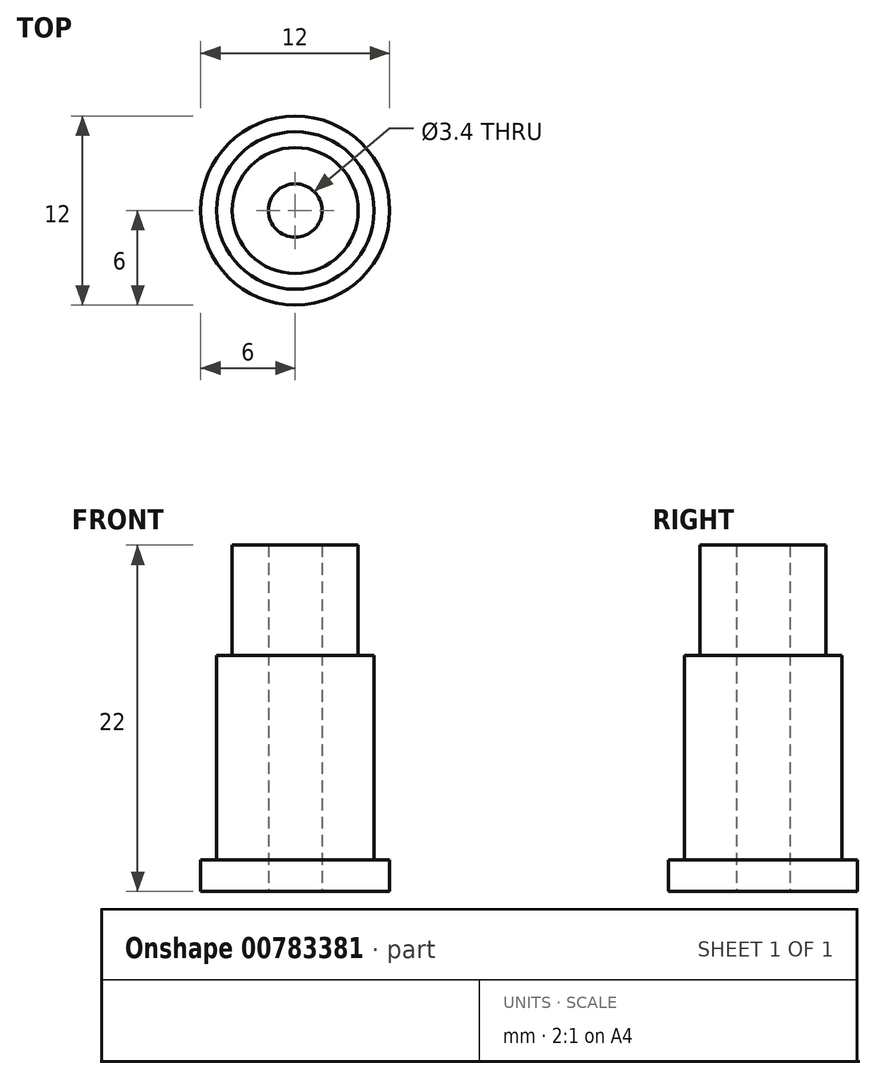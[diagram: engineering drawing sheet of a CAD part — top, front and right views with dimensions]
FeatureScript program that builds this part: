
annotation { "Feature Type Name" : "Feature", "Feature Type Description" : "" }
export const myFeature = defineFeature(function(context is Context, id is Id, definition is map)
    precondition{}
    {
        {
            var Q0;
            Q0=qCreatedBy(makeId("Top.planeOp"),FACE);
            var sketch = newSketch(context, id + "F0", { "sketchPlane" : qUnion([Q0])});
            skCircle(sketch, "E0", {"center": v(0, 0) * mm, "radius": 5 * mm});
            skCircle(sketch, "E1", {"center": v(0, 0) * mm, "radius": 4 * mm});
            skCircle(sketch, "E2", {"center": v(0, 0) * mm, "radius": 6 * mm});
            skSolve(sketch);
        }
        {
            var Q0;
            Q0=makeQuery(id+"F0.imprint","IMPRINT",FACE,{"disambiguationData":[TD([[makeQuery(id+"F0.imprint","IMPRINT",EDGE,{"derivedFrom":sQuery(id+"F0.wireOp",EDGE,"E1")}),1.0]])]});
            extrude(context, id + "F1", {"entities" : qUnion([Q0]), "depth" : 22 * mm, "offsetDistance" : 25 * mm});
        }
        {
            var Q0;
            Q0=makeQuery(id+"F0.imprint","IMPRINT",FACE,{"disambiguationData":[TD([[makeQuery(id+"F0.imprint","IMPRINT",EDGE,{"derivedFrom":sQuery(id+"F0.wireOp",EDGE,"E0")}),1.0]])]});
            extrude(context, id + "F2", {"entities" : qUnion([Q0]), "operationType" : NewBodyOperationType.ADD, "depth" : 15 * mm, "offsetDistance" : 25 * mm});
        }
        {
            var Q0;
            Q0=makeQuery(id+"F0.imprint","IMPRINT",FACE,{"disambiguationData":[TD([[makeQuery(id+"F0.imprint","IMPRINT",EDGE,{"derivedFrom":sQuery(id+"F0.wireOp",EDGE,"E0")}),-1.0]])]});
            extrude(context, id + "F3", {"entities" : qUnion([Q0]), "operationType" : NewBodyOperationType.ADD, "depth" : 2 * mm, "offsetDistance" : 25 * mm});
        }
        {
            var Q0;
            Q0=sQuery(id+"F0.wireOp",VERTEX,"E0.center");
            var Q1;
            Q1=makeQuery(id+"F1.opExtrude","SWEPT_BODY",BODY,{"disambiguationData":[OSD([sQuery(id+"F0.wireOp",EDGE,"E1")])]});
            hole(context, id + "F4", {"style" : HoleStyle.SIMPLE, "endStyle" : HoleEndStyle.THROUGH, "oppositeDirection" : true, "holeDiameter" : 3.4 * mm, "majorDiameter" : 5 * mm, "isTappedThrough" : true, "tappedDepth" : 12 * mm, "tapClearance" : 3, "locations" : qUnion([Q0]), "scope" : qUnion([Q1])});
        }
    });
